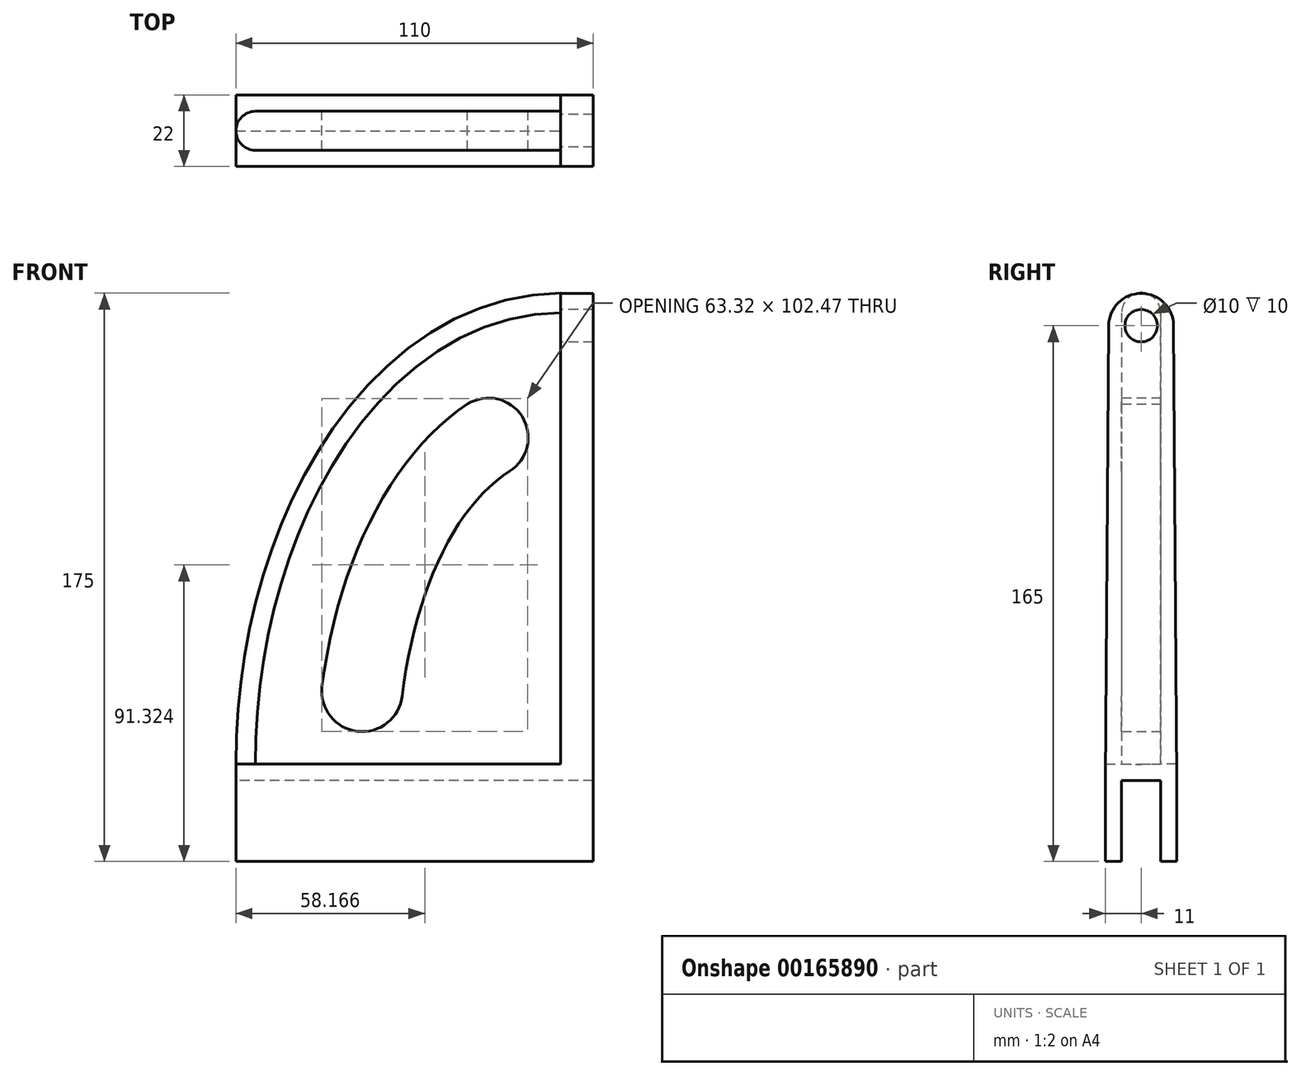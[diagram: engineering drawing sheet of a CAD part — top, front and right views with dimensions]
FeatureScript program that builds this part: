
annotation { "Feature Type Name" : "Feature", "Feature Type Description" : "" }
export const myFeature = defineFeature(function(context is Context, id is Id, definition is map)
    precondition{}
    {
        {
            var Q0;
            Q0=qCreatedBy(makeId("Right.planeOp"),FACE);
            var sketch = newSketch(context, id + "F0", { "sketchPlane" : qUnion([Q0])});
            skLineSegment(sketch, "E0", {"start": v(6, 0) * mm, "end": v(6, -25) * mm});
            skLineSegment(sketch, "E1", {"start": v(6, -25) * mm, "end": v(11, -25) * mm});
            skLineSegment(sketch, "E2", {"start": v(11, -25) * mm, "end": v(11, 0) * mm});
            skLineSegment(sketch, "E3", {"start": v(11, 0) * mm, "end": v(10, 140) * mm});
            skLineSegment(sketch, "E4.MirrorCS", {"start": v(-6, 0) * mm, "end": v(-6, -25) * mm});
            skLineSegment(sketch, "E5.MirrorCS", {"start": v(-6, -25) * mm, "end": v(-11, -25) * mm});
            skLineSegment(sketch, "E6.MirrorCS", {"start": v(-11, -25) * mm, "end": v(-11, 0) * mm});
            skLineSegment(sketch, "E7.MirrorCS", {"start": v(-11, 0) * mm, "end": v(-10, 140) * mm});
            skLineSegment(sketch, "E8", {"start": v(6, 0) * mm, "end": v(0, 0) * mm});
            skLineSegment(sketch, "E9.MirrorCS", {"start": v(-6, 0) * mm, "end": v(0, 0) * mm});
            skCircle(sketch, "E10", {"center": v(0, 140) * mm, "radius": 5 * mm});
            skArc(sketch, "E11", {"start": v(10, 140) * mm, "mid": v(0, 149.93) * mm, "end": v(-10, 140) * mm});
            skSolve(sketch);
        }
        {
            var Q0;
            Q0 = qSketchRegion(id + "F0", true);
            extrude(context, id + "F1", {"entities" : qUnion([Q0]), "depth" : 10 * mm});
        }
        {
            var Q0;
            Q0=makeQuery(id+"F1.opExtrude","CAP_FACE",FACE,{"disambiguationData":[OSD([sQuery(id+"F0.wireOp",EDGE,"E0"),sQuery(id+"F0.wireOp",EDGE,"E1"),sQuery(id+"F0.wireOp",EDGE,"E2"),sQuery(id+"F0.wireOp",EDGE,"E3"),sQuery(id+"F0.wireOp",EDGE,"E4.MirrorCS"),sQuery(id+"F0.wireOp",EDGE,"E5.MirrorCS"),sQuery(id+"F0.wireOp",EDGE,"E6.MirrorCS"),sQuery(id+"F0.wireOp",EDGE,"E7.MirrorCS"),sQuery(id+"F0.wireOp",EDGE,"E8"),sQuery(id+"F0.wireOp",EDGE,"E9.MirrorCS"),sQuery(id+"F0.wireOp",EDGE,"E10"),sQuery(id+"F0.wireOp",EDGE,"E11")])],"isStart":true});
            var sketch = newSketch(context, id + "F2", { "sketchPlane" : qUnion([Q0])});
            skLineSegment(sketch, "E12", {"start": v(0, 0) * mm, "end": v(6, 0) * mm});
            skLineSegment(sketch, "E13", {"start": v(6, 0) * mm, "end": v(6, -25) * mm});
            skLineSegment(sketch, "E14", {"start": v(6, -25) * mm, "end": v(11, -25) * mm});
            skLineSegment(sketch, "E15", {"start": v(11, -25) * mm, "end": v(11, 0) * mm});
            skLineSegment(sketch, "E16", {"start": v(11, 0) * mm, "end": v(10.96, 5) * mm});
            skLineSegment(sketch, "E17", {"start": v(10.96, 5) * mm, "end": v(0, 4.92) * mm});
            skLineSegment(sketch, "E18.MirrorCS", {"start": v(0, 0) * mm, "end": v(-6, 0) * mm});
            skLineSegment(sketch, "E19.MirrorCS", {"start": v(-6, 0) * mm, "end": v(-6, -25) * mm});
            skLineSegment(sketch, "E20.MirrorCS", {"start": v(-6, -25) * mm, "end": v(-11, -25) * mm});
            skLineSegment(sketch, "E21.MirrorCS", {"start": v(-11, -25) * mm, "end": v(-11, 0) * mm});
            skLineSegment(sketch, "E22.MirrorCS", {"start": v(-11, 0) * mm, "end": v(-10.96, 5) * mm});
            skLineSegment(sketch, "E23.MirrorCS", {"start": v(-10.96, 5) * mm, "end": v(0, 4.92) * mm});
            skSolve(sketch);
        }
        {
            var Q0;
            Q0 = qSketchRegion(id + "F2", true);
            extrude(context, id + "F3", {"entities" : qUnion([Q0]), "operationType" : NewBodyOperationType.ADD, "depth" : 100 * mm});
        }
        {
            var Q0;
            Q0=qCreatedBy(makeId("Front.planeOp"),FACE);
            var sketch = newSketch(context, id + "F4", { "sketchPlane" : qUnion([Q0])});
            skLineSegment(sketch, "E24", {"start": v(0, 150) * mm, "end": v(0, 5) * mm});
            skLineSegment(sketch, "E25", {"start": v(0, 5) * mm, "end": v(-50, 5) * mm});
            skEllipticalArc(sketch, "E26", {});
            skEllipticalArc(sketch, "E27", {});
            skPoint(sketch, "E28", {"position": v(-75, 5) * mm});
            skPoint(sketch, "E29", {"position": v(0, 125) * mm});
            skEllipticalArc(sketch, "E30", {});
            skPoint(sketch, "E31", {"position": v(0, 100) * mm});
            skPoint(sketch, "E32", {"position": v(-50, 5) * mm});
            skArc(sketch, "E33", {"start": v(-15.71, 95.19) * mm, "mid": v(-11.87, 112.02) * mm, "end": v(-28.7, 115.86) * mm});
            skLineSegment(sketch, "E34", {"start": v(-28.7, 115.86) * mm, "end": v(-15.71, 95.19) * mm, "construction": true});
            skLineSegment(sketch, "E35.trimOffspring", {"start": v(-75, 5) * mm, "end": v(-100, 5) * mm});
            skArc(sketch, "E36", {"start": v(-73.5, 28.93) * mm, "mid": v(-62.6, 15.09) * mm, "end": v(-48.77, 25.98) * mm});
            skLineSegment(sketch, "E37", {"start": v(-73.5, 28.93) * mm, "end": v(-48.77, 25.98) * mm, "construction": true});
            skLineSegment(sketch, "E38", {"start": v(-75, 5) * mm, "end": v(-50, 5) * mm});
            const initialGuessF4  = {"E26": [0, 0.004999872453860119, 0, 1, 0.1450001275461399, 0.1, 0, 1.5707963267948966], "E27": [0, 0.004999872453860119, 0, 1, 0.12000012754613988, 0.075, 0.392809654577614, 1.5707963267948966], "E30": [0, 0.004999872453860119, 0, 1, 0.09500012754613986, 0.05, 0.31961467482627687, 1.3481364639705686]};
            skSetInitialGuess(sketch, initialGuessF4);
            skSolve(sketch);
        }
        {
            var Q0;
            Q0 = qSketchRegion(id + "F4", true);
            extrude(context, id + "F5", {"entities" : qUnion([Q0]), "operationType" : NewBodyOperationType.ADD, "depth" : 6 * mm, "hasSecondDirection" : true, "secondDirectionOppositeDirection" : true, "secondDirectionDepth" : 6 * mm});
        }
        {
            var Q0;
            Q0=makeQuery(id+"F5.opExtrude","CAP_EDGE",EDGE,{"disambiguationData":[OSD([sQuery(id+"F4.wireOp",EDGE,"E26")])],"isStart":false});
            fillet(context, id + "F6", {"entities" : qUnion([Q0]), "radius" : 6 * mm, "tangentPropagation" : true, "allowEdgeOverflow" : false});
        }
        {
            var Q0;
            Q0=makeQuery(id+"F5.opExtrude","CAP_EDGE",EDGE,{"disambiguationData":[OSD([sQuery(id+"F4.wireOp",EDGE,"E26")])],"isStart":true});
            fillet(context, id + "F7", {"entities" : qUnion([Q0]), "radius" : 6 * mm, "tangentPropagation" : true, "allowEdgeOverflow" : false});
        }
    });
